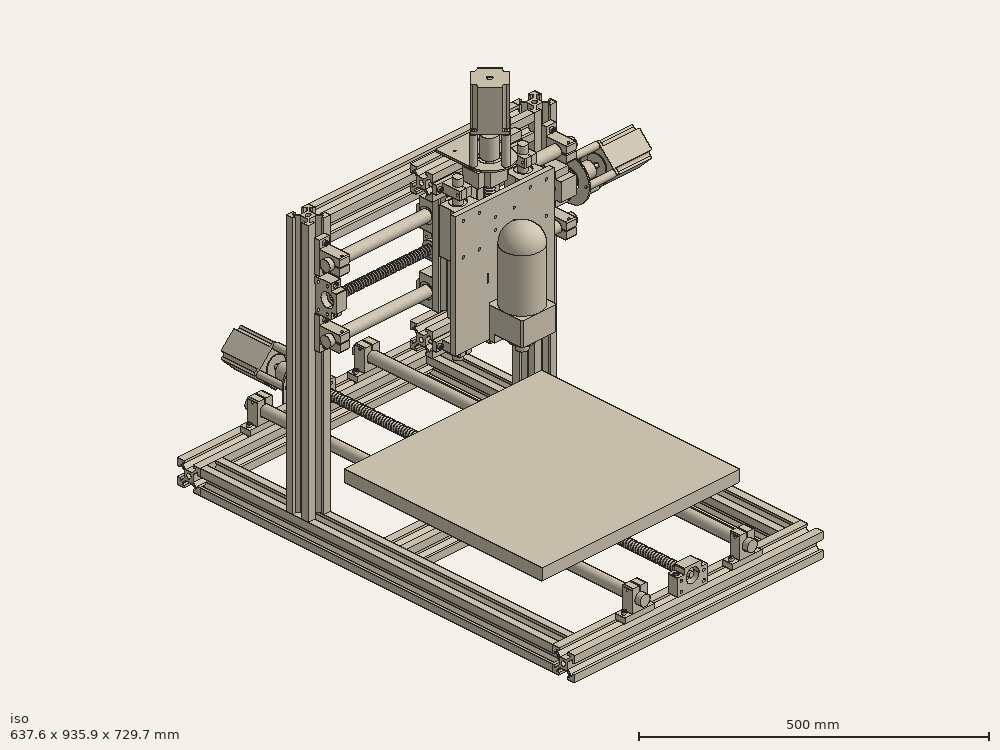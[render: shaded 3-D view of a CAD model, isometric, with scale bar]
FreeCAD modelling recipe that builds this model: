
FCSTD DOCUMENT  (FreeCAD 0.15R4671 (Git))
Label: my_first_cnc
License: CC-BY 3.0
LicenseURL: http://creativecommons.org/licenses/by/3.0/
objects: Part::Feature×111, Part::Cut×42, Part::Cylinder×16, App::DocumentObjectGroup×15, Part::Extrusion×12, PartDesign::Fillet×12, Part::Box×10, Part::Fillet×8, Part::Fuse×1, Part::MultiFuse×1
note: 213 computed .brp shape members not serialized (recipe doc carries the construction recipe); baked Part::Feature solids carry a one-line shape summary decoded from their .brp

FEATURE [Part::Cut] Cut
  Placement = pos=(150,-22,0) rot=(0,0,1;0rad)
FEATURE [Part::Cut] Cut001
  Placement = pos=(40,-22,0) rot=(0,0,1;0rad)
FEATURE [Part::Cut] Cut002
  Placement = pos=(99,-22,0) rot=(0,0,1;0rad)
FEATURE [Part::Cut] Cut003
  Placement = pos=(216,-22,0) rot=(0,0,1;0rad)
FEATURE [Part::Cut] Cut005
  Placement = pos=(332,-22,0) rot=(0,0,1;0rad)
FEATURE [Part::Cut] Cut006
  Placement = pos=(272,-22,0) rot=(0,0,1;0rad)
FEATURE [Part::Extrusion] Extrude002  label="Left"
  Base = -> Cut002
  Dir = (0,0,713)
  Placement = pos=(620.51,-22.0046,-22.0002) rot=(-1,0,0;1.5708rad)
  Solid = false
FEATURE [Part::Cut] Cut004
  Placement = pos=(161,-22,0) rot=(0,0,1;0rad)
FEATURE [Part::Extrusion] Extrude003  label="Right"
  Base = -> Cut004
  Dir = (0,0,713)
  Placement = pos=(1016.51,-22.0045,-22) rot=(-1,0,0;1.5708rad)
  Solid = false
FEATURE [Part::Extrusion] Extrude004  label="Back"
  Base = -> Cut003
  Dir = (0,0,503)
  Placement = pos=(719.51,757.995,260.93) rot=(0,1,0;1.5708rad)
  Solid = false
FEATURE [Part::Extrusion] Extrude005  label="Front"
  Base = -> Cut006
  Dir = (0,0,503)
  Placement = pos=(719.51,-0.00457416,317) rot=(0,1,0;1.5708rad)
  Solid = false
FEATURE [Part::Cut] Cut007
  Placement = pos=(399,-22,0) rot=(0,0,1;0rad)
FEATURE [Part::Cut] Cut008
  Placement = pos=(451,-22,0) rot=(0,0,1;0rad)
FEATURE [Part::Extrusion] Extrude006  label="Inner_base"
  Base = -> Cut005
  Dir = (0,0,413)
  Placement = pos=(764.5,385,377.214) rot=(0,1,0;1.5708rad)
  Solid = false
FEATURE [Part::Extrusion] Extrude009  label="Inner_gantry"
  Dir = (0,0,413)
  Placement = pos=(764.516,538.755,866.83) rot=(0,1,0;1.5708rad)
  Solid = false
FEATURE [Part::Extrusion] Extrude010  label="gantry_left"
  Base = -> Cut007
  Dir = (0,0,490)
  Placement = pos=(320.516,538.755,44.85) rot=(0,0,1;0rad)
  Solid = false
FEATURE [Part::Extrusion] Extrude011  label="gantry_right"
  Base = -> Cut008
  Dir = (0,0,490)
  Placement = pos=(726.5,538.755,44.8) rot=(0,0,1;0rad)
  Solid = false
FEATURE [Part::Cylinder] Cylinder  label="Shaft_Z_Right"
  Angle = 360
  Height = 300
  Placement = pos=(1029.9,347.799,295.468) rot=(0,0,1;0rad)
  Radius = 8
FEATURE [Part::Cylinder] Cylinder001  label="Shaft_Z_Left"
  Angle = 360
  Height = 300
  Placement = pos=(897.986,347.799,294.632) rot=(0,0,1;0rad)
  Radius = 8
FEATURE [Part::Cylinder] Cylinder002  label="Shaft_Y_Top"
  Angle = 360
  Height = 500
  Placement = pos=(722.44,440.799,480.216) rot=(0,1,0;1.5708rad)
  Radius = 10
FEATURE [Part::Cylinder] Cylinder003  label="Shaft_Y_Bottom"
  Angle = 360
  Height = 500
  Placement = pos=(722.44,439.847,355.335) rot=(0,1,0;1.5708rad)
  Radius = 10
FEATURE [Part::Cylinder] Cylinder004  label="Shaft_X_Left"
  Angle = 360
  Height = 800
  Placement = pos=(864.2,-65.0507,76.25) rot=(-1,0,0;1.5708rad)
  Radius = 10
FEATURE [Part::Cylinder] Cylinder005  label="Shaft_X_Right"
  Angle = 360
  Height = 800
  Placement = pos=(1082.5,-64,76.25) rot=(-1,0,0;1.5708rad)
  Radius = 10
FEATURE [Part::Box] Box001
  Height = 10
  Length = 60
  Width = 20
FEATURE [Part::Fuse] Fusion
  Base = -> Box001
FEATURE [Part::Cylinder] Cylinder007
  Angle = 360
  Height = 13
  Placement = pos=(7.5,10,-2) rot=(0,0,1;0rad)
  Radius = 2.3
FEATURE [Part::Cut] Cut010
  Base = -> Fusion
  Tool = -> Cylinder007
FEATURE [Part::Cylinder] Cylinder008
  Angle = 360
  Height = 13
  Placement = pos=(52.5,10,-2) rot=(0,0,1;0rad)
  Radius = 2.3
FEATURE [Part::Cut] Cut011
  Base = -> Cut010
  Tool = -> Cylinder008
FEATURE [Part::Cylinder] Cylinder009
  Angle = 360
  Height = 33
  Placement = pos=(13.1208,9.89392,45.5993) rot=(0,1,0;1.5708rad)
  Radius = 2.3
FEATURE [Part::Cut] Cut012
  Base = -> Cut011
  Tool = -> Cylinder009
FEATURE [Part::Box] Box003
  Height = 15
  Length = 2
  Placement = pos=(29,-2.73,37.37) rot=(0,0,1;0rad)
  Width = 25
FEATURE [Part::Cut] Cut013  label="SK20_X_Front_Left"
  Base = -> Cut012
  Placement = pos=(834.178,-54.56,45.2) rot=(0,0,1;0rad)
  Tool = -> Box003
FEATURE [Part::Cut] Cut014  label="SK020_X_Front_Right"
  Placement = pos=(1051.53,-54.56,45.2) rot=(0,0,1;0rad)
FEATURE [Part::Cut] Cut015  label="SK020_X_Back_Left"
  Placement = pos=(834.409,704.33,45.1) rot=(0,0,1;0rad)
FEATURE [Part::Cut] Cut016  label="SK020_X_Back_Right"
  Placement = pos=(1051.28,704.33,45.1) rot=(0,0,1;0rad)
FEATURE [Part::Cut] Cut017  label="SK020_Y_Bottom_Right"
  Placement = pos=(1190.11,470.93,385) rot=(0.57735,0.57735,-0.57735;2.0944rad)
FEATURE [Part::Cut] Cut018  label="SK020_Y_Top_Right"
  Placement = pos=(1190.95,471.863,510.292) rot=(0.57735,0.57735,-0.57735;2.0944rad)
FEATURE [Part::Cut] Cut019  label="SK020_Y_Bottom_Left"
  Placement = pos=(732.2,471.295,385) rot=(0.57735,0.57735,-0.57735;2.0944rad)
FEATURE [Part::Cut] Cut020  label="SK020_Y_Top_Left"
  Placement = pos=(732.1,471.774,510.292) rot=(0.57735,0.57735,-0.57735;2.0944rad)
FEATURE [Part::Box] Box004  label="Bed"
  Height = 22
  Length = 400
  Placement = pos=(775.334,50.53,98.54) rot=(0,0,1;0rad)
  Width = 400
FEATURE [Part::Feature] M6_Tnut_slot
  Placement = pos=(844.753,-45.1982,38.5832) rot=(0.57735,0.57735,0.57735;2.0944rad)
  shape: bbox 10 x 19.6 x 9.67 mm, 55 faces, 0 solids (baked)
FEATURE [Part::Feature] M6_Tnut_slot001
  Placement = pos=(886.7,-45.8436,38.583) rot=(0.57735,0.57735,0.57735;2.0944rad)
  shape: bbox 10 x 19.6 x 9.67 mm, 55 faces, 0 solids (baked)
FEATURE [Part::Feature] M6_Tnut_slot002
  Placement = pos=(1104.18,-44.84,38.5834) rot=(0.57735,0.57735,0.57735;2.0944rad)
  shape: bbox 10 x 19.6 x 9.67 mm, 55 faces, 0 solids (baked)
FEATURE [Part::Feature] M6_Tnut_slot003
  Placement = pos=(1059,-43.9078,38.5833) rot=(0.57735,0.57735,0.57735;2.0944rad)
  shape: bbox 10 x 19.6 x 9.67 mm, 55 faces, 0 solids (baked)
FEATURE [Part::Feature] M6_Tnut_slot004
  Placement = pos=(841.887,713.889,38.724) rot=(0.57735,0.57735,0.57735;2.0944rad)
  shape: bbox 10 x 19.6 x 9.67 mm, 55 faces, 0 solids (baked)
FEATURE [Part::Feature] M6_Tnut_slot005
  Placement = pos=(1200.15,477.74,332.424) rot=(0,0,1;3.14159rad)
  shape: bbox 19.6 x 9.67 x 10 mm, 55 faces, 0 solids (baked)
FEATURE [Part::Feature] M6_Tnut_slot006
  Placement = pos=(887.231,713.888,38.7233) rot=(0.57735,0.57735,0.57735;2.0944rad)
  shape: bbox 10 x 19.6 x 9.67 mm, 55 faces, 0 solids (baked)
FEATURE [Part::Feature] M6_Tnut_slot007
  Placement = pos=(1058.64,714.392,38.7233) rot=(0.57735,0.57735,0.57735;2.0944rad)
  shape: bbox 10 x 19.6 x 9.67 mm, 55 faces, 0 solids (baked)
FEATURE [Part::Feature] M6_Tnut_slot008
  Placement = pos=(1103.91,714.392,38.7233) rot=(0.57735,0.57735,0.57735;2.0944rad)
  shape: bbox 10 x 19.6 x 9.67 mm, 55 faces, 0 solids (baked)
FEATURE [Part::Feature] M6_Tnut_slot009
  Placement = pos=(1200.11,477.74,377.562) rot=(0,0,1;3.14159rad)
  shape: bbox 19.6 x 9.67 x 10 mm, 55 faces, 0 solids (baked)
FEATURE [Part::Feature] M6_Tnut_slot010
  Placement = pos=(1200.95,476.213,457.743) rot=(0,0,1;3.14159rad)
  shape: bbox 19.6 x 9.67 x 10 mm, 55 faces, 0 solids (baked)
FEATURE [Part::Feature] M6_Tnut_slot011
  Placement = pos=(1200.95,476.213,502.749) rot=(0,0,1;3.14159rad)
  shape: bbox 19.6 x 9.67 x 10 mm, 55 faces, 0 solids (baked)
FEATURE [Part::Feature] M6_Tnut_slot012
  Placement = pos=(742.302,476.923,502.73) rot=(0,0,1;3.14159rad)
  shape: bbox 19.6 x 9.67 x 10 mm, 55 faces, 0 solids (baked)
FEATURE [Part::Feature] M6_Tnut_slot013
  Placement = pos=(742.504,477.741,457.628) rot=(0,0,1;3.14159rad)
  shape: bbox 19.6 x 9.67 x 10 mm, 55 faces, 0 solids (baked)
FEATURE [Part::Feature] M6_Tnut_slot014
  Placement = pos=(742.302,477.742,376.507) rot=(0,0,1;3.14159rad)
  shape: bbox 19.6 x 9.67 x 10 mm, 55 faces, 0 solids (baked)
FEATURE [Part::Feature] M6_Tnut_slot015
  Placement = pos=(742.328,477.738,332.439) rot=(0,0,1;3.14159rad)
  shape: bbox 19.6 x 9.67 x 10 mm, 55 faces, 0 solids (baked)
FEATURE [Part::Cut] Cut021  label="Cut013"
  Placement = pos=(220,-22,0) rot=(0,0,1;0rad)
FEATURE [Part::Cut] Cut022  label="Cut014"
  Placement = pos=(-22,-22,0) rot=(0,0,1;0rad)
FEATURE [Part::Extrusion] Extrude013  label="Right_Z"
  Base = -> Cut001
  Dir = (0,0,213)
  Placement = pos=(924.038,442,336.783) rot=(0,0,1;0rad)
  Solid = false
FEATURE [Part::Extrusion] Extrude014  label="Left_Z"
  Base = -> Cut022
  Dir = (0,0,213)
  Placement = pos=(940.038,442,336.783) rot=(0,0,1;0rad)
  Solid = false
FEATURE [Part::Cut] Cut036  label="SC20VUU004"
  Placement = pos=(955,420,507.314) rot=(0.57735,-0.57735,-0.57735;4.18879rad)
FEATURE [Part::Cut] Cut037  label="SC20VUU005"
  Placement = pos=(1000.5,420,507.275) rot=(0.57735,-0.57735,-0.57735;4.18879rad)
FEATURE [Part::Cut] Cut038  label="SC20VUU006"
  Placement = pos=(955,420,382.628) rot=(0.57735,-0.57735,-0.57735;4.18879rad)
FEATURE [Part::Cut] Cut039  label="SC20VUU007"
  Placement = pos=(1000.5,420,382.412) rot=(0.57735,-0.57735,-0.57735;4.18879rad)
FEATURE [Part::Cut] Cut040  label="Cut032"
  Placement = pos=(54.0681,-22,14.7162) rot=(0,0,1;0rad)
FEATURE [Part::Cut] Cut041  label="Cut033"
  Placement = pos=(-24.4873,-22.0001,-16.5816) rot=(0,0,1;0rad)
FEATURE [Part::Extrusion] Extrude016  label="Top_Z"
  Base = -> Cut040
  Dir = (0,0,180)
  Placement = pos=(859.038,442,649.933) rot=(0,1,0;1.5708rad)
  Solid = false
FEATURE [Part::Extrusion] Extrude017  label="Bottom_Z"
  Base = -> Cut041
  Dir = (0,0,180)
  Placement = pos=(890.317,442,312.344) rot=(0,1,0;1.5708rad)
  Solid = false
FEATURE [PartDesign::Fillet] Fillet
  Base = -> Cut020 [Edge39]
  Radius = 2
FEATURE [PartDesign::Fillet] Fillet001
  Base = -> Fillet [Edge35]
  Radius = 2
FEATURE [PartDesign::Fillet] Fillet004
  Base = -> Cut018 [Edge39]
  Radius = 2
FEATURE [PartDesign::Fillet] Fillet005
  Base = -> Fillet004 [Edge35]
  Radius = 2
FEATURE [PartDesign::Fillet] Fillet008
  Base = -> Cut015 [Edge52]
  Placement = pos=(834.409,704.33,45.1) rot=(0,0,1;0rad)
  Radius = 2
FEATURE [PartDesign::Fillet] Fillet009
  Base = -> Fillet008 [Edge28]
  Placement = pos=(834.409,704.33,45.1) rot=(0,0,1;0rad)
  Radius = 2
FEATURE [PartDesign::Fillet] Fillet010
  Base = -> Cut016 [Edge39]
  Placement = pos=(1051.28,704.33,45.1) rot=(0,0,1;0rad)
  Radius = 2
FEATURE [PartDesign::Fillet] Fillet011
  Base = -> Fillet010 [Edge35]
  Placement = pos=(1051.28,704.33,45.1) rot=(0,0,1;0rad)
  Radius = 2
FEATURE [PartDesign::Fillet] Fillet012
  Base = -> Cut014 [Edge52]
  Placement = pos=(1051.53,-54.56,45.2) rot=(0,0,1;0rad)
  Radius = 2
FEATURE [PartDesign::Fillet] Fillet013
  Base = -> Fillet012 [Edge28]
  Placement = pos=(1051.53,-54.56,45.2) rot=(0,0,1;0rad)
  Radius = 2
FEATURE [PartDesign::Fillet] Fillet014
  Base = -> Cut013 [Edge52]
  Placement = pos=(834.178,-54.56,45.2) rot=(0,0,1;0rad)
  Radius = 2
FEATURE [PartDesign::Fillet] Fillet015
  Base = -> Fillet014 [Edge28]
  Placement = pos=(834.178,-54.56,45.2) rot=(0,0,1;0rad)
  Radius = 2
FEATURE [Part::Fillet] Fillet001002
  Edges = 1 edges r=2: [Edge27]
  Placement = pos=(1053.67,374.8,581.619) rot=(0,0.707107,-0.707107;3.14159rad)
FEATURE [Part::Fillet] Fillet001003
  Edges = 1 edges r=2: [Edge27]
  Placement = pos=(921.74,374.8,322.412) rot=(0,0.707107,-0.707107;3.14159rad)
FEATURE [Part::Fillet] Fillet001004
  Edges = 1 edges r=2: [Edge27]
  Placement = pos=(1053.77,374.8,322.519) rot=(0,0.707107,-0.707107;3.14159rad)
FEATURE [Part::Fillet] Fillet001005
  Edges = 1 edges r=2: [Edge27]
  Placement = pos=(921.98,374.8,581.619) rot=(0,0.707107,-0.707107;3.14159rad)
FEATURE [Part::Box] Box012
  Height = 32.5
  Length = 50
  Width = 85
FEATURE [Part::Cylinder] Cylinder015
  Angle = 360
  Height = 100
  Placement = pos=(25,-4.78696,19) rot=(-1,0,0;1.5708rad)
  Radius = 8.1
FEATURE [Part::Cut] Cut042
  Base = -> Box012
  Tool = -> Cylinder015
FEATURE [Part::Box] Box001001
  Height = 6
  Length = 25
  Placement = pos=(-43.8255,-3.33042e-05,2.24746) rot=(0,0,1;0rad)
  Width = 85
FEATURE [Part::Box] Box002001
  Height = 10
  Length = 10
  Placement = pos=(-50.8986,-3,9.31859) rot=(0,1,0;0.785397rad)
  Width = 90
FEATURE [Part::Cut] Cut001001
  Base = -> Box001001
  Tool = -> Box002001
FEATURE [Part::Box] Box003001
  Height = 10
  Length = 10
  Placement = pos=(-18.82,-2,2.25) rot=(0,-1,0;0.785397rad)
  Width = 90
FEATURE [Part::Cut] Cut002001
  Base = -> Cut001001
  Placement = pos=(56.6969,-0.000184233,30.2) rot=(0,0,1;0rad)
  Tool = -> Box003001
FEATURE [Part::MultiFuse] Fusion002
  Shapes = -> [Cut042,Cut002001]
FEATURE [Part::Box] Box004001
  Height = 23.5
  Length = 1
  Placement = pos=(0,0,9) rot=(0,0,1;0rad)
  Width = 85
FEATURE [Part::Cut] Cut003001
  Base = -> Fusion002
  Tool = -> Box004001
FEATURE [Part::Box] Box005001
  Height = 23.5
  Length = 1
  Placement = pos=(49,0,9) rot=(0,0,1;0rad)
  Width = 85
FEATURE [Part::Cut] Cut004001
  Base = -> Cut003001
  Tool = -> Box005001
FEATURE [Part::Cylinder] Cylinder001001
  Angle = 360
  Height = 40
  Placement = pos=(7,12.5,-2) rot=(0,0,1;0rad)
  Radius = 2.3
FEATURE [Part::Cut] Cut005001
  Base = -> Cut004001
  Tool = -> Cylinder001001
FEATURE [Part::Cylinder] Cylinder002001
  Angle = 360
  Height = 40
  Placement = pos=(7,72.5,-3) rot=(0,0,1;0rad)
  Radius = 2.3
FEATURE [Part::Cut] Cut006001
  Base = -> Cut005001
  Tool = -> Cylinder002001
FEATURE [Part::Cylinder] Cylinder003001
  Angle = 360
  Height = 40
  Placement = pos=(43,12.5,-4) rot=(0,0,1;0rad)
  Radius = 2
FEATURE [Part::Cut] Cut007001
  Base = -> Cut006001
  Tool = -> Cylinder003001
FEATURE [Part::Cylinder] Cylinder004001
  Angle = 360
  Height = 40
  Placement = pos=(43,72.5,-4) rot=(0,0,1;0rad)
  Radius = 2.3
FEATURE [Part::Cut] Cut008001
  Base = -> Cut007001
  Tool = -> Cylinder004001
FEATURE [Part::Cylinder] Cylinder005001
  Angle = 360
  Height = 3
  Placement = pos=(25.5737,-1,19.0038) rot=(-1,0,0;1.5708rad)
  Radius = 14
FEATURE [Part::Cut] Cut009001
  Base = -> Cut008001
  Tool = -> Cylinder005001
FEATURE [Part::Cut] Cut010001
  Base = -> Cut009001
  Tool = -> Cylinder005001
FEATURE [Part::Cylinder] Cylinder006001
  Angle = 360
  Height = 3
  Placement = pos=(25.6346,83,19.0294) rot=(-1,0,0;1.5708rad)
  Radius = 14
FEATURE [Part::Cut] Cut011001
  Base = -> Cut010001
  Placement = pos=(872.932,328.758,552.688) rot=(-1,0,0;1.5708rad)
  Tool = -> Cylinder006001
FEATURE [Part::Cut] Cut011002
  Placement = pos=(1004.97,328.822,552.619) rot=(-1,0,0;1.5708rad)
FEATURE [Part::Feature] M6_Tnut_slot10
  Placement = pos=(879.631,381.008,573.739) rot=(0.707107,0,0.707107;3.14159rad)
  shape: bbox 10 x 9.67 x 19.6 mm, 55 faces, 0 solids (baked)
FEATURE [Part::Feature] M6_Tnut_slot016
  Placement = pos=(916.2,381.031,573.724) rot=(0.707107,0,0.707107;3.14159rad)
  shape: bbox 10 x 9.67 x 19.6 mm, 55 faces, 0 solids (baked)
FEATURE [Part::Feature] M6_Tnut_slot017
  Placement = pos=(1011.45,381.019,573.726) rot=(0.707107,0,0.707107;3.14159rad)
  shape: bbox 10 x 9.67 x 19.6 mm, 55 faces, 0 solids (baked)
FEATURE [Part::Feature] M6_Tnut_slot018
  Placement = pos=(1047.94,381.016,573.724) rot=(0.707107,0,0.707107;3.14159rad)
  shape: bbox 10 x 9.67 x 19.6 mm, 55 faces, 0 solids (baked)
FEATURE [Part::Feature] M6_Tnut_slot020
  Placement = pos=(879.473,380.903,314.506) rot=(0.707107,0,0.707107;3.14159rad)
  shape: bbox 10 x 9.67 x 19.6 mm, 55 faces, 0 solids (baked)
FEATURE [Part::Feature] M6_Tnut_slot021
  Placement = pos=(916.005,380.953,314.519) rot=(0.707107,0,0.707107;3.14159rad)
  shape: bbox 10 x 9.67 x 19.6 mm, 55 faces, 0 solids (baked)
FEATURE [Part::Feature] M6_Tnut_slot022
  Placement = pos=(1011.52,380.955,314.598) rot=(0.707107,0,0.707107;3.14159rad)
  shape: bbox 10 x 9.67 x 19.6 mm, 55 faces, 0 solids (baked)
FEATURE [Part::Feature] M6_Tnut_slot023
  Placement = pos=(1048.04,380.934,314.688) rot=(0.707107,0,0.707107;3.14159rad)
  shape: bbox 10 x 9.67 x 19.6 mm, 55 faces, 0 solids (baked)
FEATURE [Part::Feature] M6_Tnut_slot024
  Placement = pos=(986.716,413.96,459.779) rot=(0,0,1;0rad)
  shape: bbox 19.6 x 9.67 x 10 mm, 55 faces, 0 solids (baked)
FEATURE [Part::Feature] M6_Tnut_slot025
  Placement = pos=(986.711,413.96,500.798) rot=(0,0,1;0rad)
  shape: bbox 19.6 x 9.67 x 10 mm, 55 faces, 0 solids (baked)
FEATURE [Part::Feature] M6_Tnut_slot026
  Placement = pos=(941.238,413.955,500.893) rot=(0,0,1;0rad)
  shape: bbox 19.6 x 9.67 x 10 mm, 55 faces, 0 solids (baked)
FEATURE [Part::Feature] M6_Tnut_slot027
  Placement = pos=(941.292,413.965,459.839) rot=(0,0,1;0rad)
  shape: bbox 19.6 x 9.67 x 10 mm, 55 faces, 0 solids (baked)
FEATURE [Part::Feature] M6_Tnut_slot028
  Placement = pos=(986.758,413.959,375.695) rot=(0,0,1;0rad)
  shape: bbox 19.6 x 9.67 x 10 mm, 55 faces, 0 solids (baked)
FEATURE [Part::Feature] M6_Tnut_slot029
  Placement = pos=(986.679,413.961,335.402) rot=(0,0,1;0rad)
  shape: bbox 19.6 x 9.67 x 10 mm, 55 faces, 0 solids (baked)
FEATURE [Part::Feature] M6_Tnut_slot030
  Placement = pos=(941.357,413.961,376.087) rot=(0,0,1;0rad)
  shape: bbox 19.6 x 9.67 x 10 mm, 55 faces, 0 solids (baked)
FEATURE [Part::Feature] M6_Tnut_slot031
  Placement = pos=(941.312,413.956,335.16) rot=(0,0,1;0rad)
  shape: bbox 19.6 x 9.67 x 10 mm, 55 faces, 0 solids (baked)
FEATURE [Part::Feature] ISO4762_M5x20_
  Placement = pos=(1104.13,-44.63,55.35) rot=(0,0,1;0rad)
  shape: bbox 9.2 x 9.2 x 25 mm, 23 faces (baked)
FEATURE [Part::Feature] ISO4762_M5x20_001
  Placement = pos=(1058.54,-44.63,55.35) rot=(0,0,1;0rad)
  shape: bbox 9.2 x 9.2 x 25 mm, 23 faces (baked)
FEATURE [Part::Feature] ISO4762_M5x20_002
  Placement = pos=(887.559,-44.6308,55.35) rot=(0,0,1;0rad)
  shape: bbox 9.2 x 9.2 x 25 mm, 23 faces (baked)
FEATURE [Part::Feature] ISO4762_M5x20_003
  Placement = pos=(841.861,-44.6304,55.35) rot=(0,0,1;0rad)
  shape: bbox 9.2 x 9.2 x 25 mm, 23 faces (baked)
FEATURE [Part::Feature] ISO4762_M5x20_004
  Placement = pos=(1103.9,714.044,55.2898) rot=(0,0,1;0rad)
  shape: bbox 9.2 x 9.2 x 25 mm, 23 faces (baked)
FEATURE [Part::Feature] ISO4762_M5x20_005
  Placement = pos=(1057.98,714.049,55.4021) rot=(0,0,1;0rad)
  shape: bbox 9.2 x 9.2 x 25 mm, 23 faces (baked)
FEATURE [Part::Feature] ISO4762_M5x20_006
  Placement = pos=(886.949,714.123,55.3565) rot=(0,0,1;0rad)
  shape: bbox 9.2 x 9.2 x 25 mm, 23 faces (baked)
FEATURE [Part::Feature] ISO4762_M5x20_007
  Placement = pos=(841.94,714.052,55.283) rot=(0,0,1;0rad)
  shape: bbox 9.2 x 9.2 x 25 mm, 23 faces (baked)
FEATURE [Part::Feature] ISO4762_M5x20_008
  Placement = pos=(1200.95,461.863,502.419) rot=(1,0,0;1.5708rad)
  shape: bbox 9.2 x 25 x 9.2 mm, 23 faces (baked)
FEATURE [Part::Feature] ISO4762_M5x20_009
  Placement = pos=(1200.95,461.663,457.226) rot=(1,0,0;1.5708rad)
  shape: bbox 9.2 x 25 x 9.2 mm, 23 faces (baked)
FEATURE [Part::Feature] ISO4762_M5x20_010
  Placement = pos=(742.076,462.099,502.511) rot=(1,0,0;1.5708rad)
  shape: bbox 9.2 x 25 x 9.2 mm, 23 faces (baked)
FEATURE [Part::Feature] ISO4762_M5x20_011
  Placement = pos=(742.071,462.002,457.208) rot=(1,0,0;1.5708rad)
  shape: bbox 9.2 x 25 x 9.2 mm, 23 faces (baked)
FEATURE [Part::Feature] ISO4762_M5x20_012
  Placement = pos=(742.121,461.12,376.304) rot=(1,0,0;1.5708rad)
  shape: bbox 9.2 x 25 x 9.2 mm, 23 faces (baked)
FEATURE [Part::Feature] ISO4762_M5x20_013
  Placement = pos=(742.163,461.12,332.014) rot=(1,0,0;1.5708rad)
  shape: bbox 9.2 x 25 x 9.2 mm, 23 faces (baked)
FEATURE [Part::Feature] ISO4762_M5x20_014
  Placement = pos=(1200,461.12,377.476) rot=(1,0,0;1.5708rad)
  shape: bbox 9.2 x 25 x 9.2 mm, 23 faces (baked)
FEATURE [Part::Feature] ISO4762_M5x20_015
  Placement = pos=(1200.11,461.099,332.483) rot=(1,0,0;1.5708rad)
  shape: bbox 9.2 x 25 x 9.2 mm, 23 faces (baked)
FEATURE [Part::Feature] ISO4762_M5x20_016
  Placement = pos=(879.79,366.7,573.653) rot=(1,0,0;1.5708rad)
  shape: bbox 9.2 x 25 x 9.2 mm, 23 faces (baked)
FEATURE [Part::Feature] ISO4762_M5x20_017
  Placement = pos=(916.367,366.7,573.47) rot=(1,0,0;1.5708rad)
  shape: bbox 9.2 x 25 x 9.2 mm, 23 faces (baked)
FEATURE [Part::Feature] ISO4762_M5x20_018
  Placement = pos=(1011.46,366.7,573.505) rot=(1,0,0;1.5708rad)
  shape: bbox 9.2 x 25 x 9.2 mm, 23 faces (baked)
FEATURE [Part::Feature] ISO4762_M5x20_019
  Placement = pos=(1047.88,366.7,573.7) rot=(1,0,0;1.5708rad)
  shape: bbox 9.2 x 25 x 9.2 mm, 23 faces (baked)
FEATURE [Part::Feature] ISO4762_M5x20_020
  Placement = pos=(879.525,366.7,314.408) rot=(1,0,0;1.5708rad)
  shape: bbox 9.2 x 25 x 9.2 mm, 23 faces (baked)
FEATURE [Part::Feature] ISO4762_M5x20_021
  Placement = pos=(915.996,366.7,314.466) rot=(1,0,0;1.5708rad)
  shape: bbox 9.2 x 25 x 9.2 mm, 23 faces (baked)
FEATURE [Part::Feature] ISO4762_M5x20_022
  Placement = pos=(1011.46,366.7,314.503) rot=(1,0,0;1.5708rad)
  shape: bbox 9.2 x 25 x 9.2 mm, 23 faces (baked)
FEATURE [Part::Feature] ISO4762_M5x20_023
  Placement = pos=(1048.08,366.7,314.536) rot=(1,0,0;1.5708rad)
  shape: bbox 9.2 x 25 x 9.2 mm, 23 faces (baked)
FEATURE [Part::Box] Box005002  label="Cube"
  Height = 10
  Length = 361
  Placement = pos=(795.534,71.3936,98.4922) rot=(0,0,1;0rad)
  Width = 361
FEATURE [Part::Cut] Cut011005  label="Spoilboard_Bed"
  Base = -> Box004
  Placement = pos=(-4.73697,-1.00343,1.16107) rot=(0,0,1;0rad)
  Tool = -> Box005002
FEATURE [Part::Feature] Pad001  label="Motor_X"
  Placement = pos=(972.86,868.93,69.8262) rot=(0.382683,0,0.92388;3.14159rad)
  shape: bbox 79.62 x 102 x 79.62 mm, 34 faces (baked)
FEATURE [Part::Feature] Pad002  label="Motor_Y"
  Placement = pos=(1357.09,446.522,417.405) rot=(0.357407,-0.357407,0.862856;1.71777rad)
  shape: bbox 102 x 79.62 x 79.62 mm, 34 faces (baked)
FEATURE [Part::Feature] Pad  label="Motor_Z"
  Placement = pos=(964.751,349.979,729.656) rot=(-0.862856,-0.357407,0.357407;1.71777rad)
  shape: bbox 79.62 x 79.62 x 102 mm, 34 faces (baked)
FEATURE [Part::Feature] Part__Feature  label="BF12_Z"
  Placement = pos=(964.673,349.918,314.167) rot=(0,0,1;3.14159rad)
  shape: bbox 60 x 43 x 20 mm, 48 faces (baked)
FEATURE [Part::Feature] Part__Feature001  label="BF12_X"
  Placement = pos=(971.01,-44.5,70.0662) rot=(0,0.707107,0.707107;3.14159rad)
  shape: bbox 60 x 20 x 43 mm, 48 faces (baked)
FEATURE [Part::Feature] Part__Feature002  label="BF12_Y"
  Placement = pos=(742.761,446.587,417.281) rot=(0.707107,0.001737,0.707104;3.14159rad)
  shape: bbox 20.11 x 43.16 x 60.08 mm, 48 faces (baked)
FEATURE [Part::Feature] Pocket  label="Motor_Holder_X"
  Placement = pos=(973.206,738.696,-0.0697632) rot=(1,0,0;1.5708rad)
  shape: bbox 80 x 2.7 x 110.1 mm, 12 faces (baked)
FEATURE [Part::Feature] Pocket001  label="Motor_Holder_Z"
  Placement = pos=(964.724,420.024,598.846) rot=(1,0,0;3.14159rad)
  shape: bbox 80 x 110.1 x 2.7 mm, 12 faces (baked)
FEATURE [Part::Feature] Pocket002  label="Motor_Holder_Y"
  Placement = pos=(1222.9,516.706,417.427) rot=(0.707107,0,0.707107;3.14159rad)
  shape: bbox 2.7 x 110.1 x 80 mm, 12 faces (baked)
FEATURE [Part::Fillet] Fillet001006
  Base = -> Cut017
  Edges = 1 edges r=2: [Edge39]
FEATURE [Part::Fillet] Fillet001007
  Base = -> Fillet001006
  Edges = 1 edges r=2: [Edge35]
FEATURE [Part::Fillet] Fillet001008
  Base = -> Cut019
  Edges = 1 edges r=2: [Edge52]
FEATURE [Part::Fillet] Fillet001009
  Base = -> Fillet001008
  Edges = 1 edges r=2: [Edge28]
FEATURE [Part::Feature] Pocket003  label="Router"
  Placement = pos=(964.205,318.53,338.088) rot=(0,0,1;3.14159rad)
  shape: bbox 70 x 70 x 208.5 mm, 23 faces (baked)
FEATURE [App::DocumentObjectGroup] Group  label="Base"
  Group = -> [Extrude002,Extrude003,Extrude004,Extrude005,Extrude006,Fillet015,Fillet013,Fillet009,Fillet011,ISO4762_M5x20_007,M6_Tnut_slot004,ISO4762_M5x20_006,M6_Tnut_slot006,M6_Tnut_slot007,ISO4762_M5x20_005,M6_Tnut_slot008,ISO4762_M5x20_004,ISO4762_M5x20_003,M6_Tnut_slot,ISO4762_M5x20_002,M6_Tnut_slot001,ISO4762_M5x20_001,M6_Tnut_slot003,ISO4762_M5x20_,M6_Tnut_slot002]
FEATURE [App::DocumentObjectGroup] Group001  label="Gantry"
  Group = -> [Extrude009,Extrude010,Extrude011,Fillet001,Fillet005,Fillet001007,Fillet001009,ISO4762_M5x20_010,M6_Tnut_slot012,ISO4762_M5x20_011,M6_Tnut_slot013,ISO4762_M5x20_008,M6_Tnut_slot011,ISO4762_M5x20_009,M6_Tnut_slot010,ISO4762_M5x20_012,M6_Tnut_slot014,ISO4762_M5x20_013,M6_Tnut_slot015,ISO4762_M5x20_014,M6_Tnut_slot009,ISO4762_M5x20_015,M6_Tnut_slot005]
FEATURE [App::DocumentObjectGroup] Group003  label="Head"
  Group = -> [Extrude016,Extrude017,Extrude013,Extrude014,Fillet001005,Fillet001002,Fillet001003,Fillet001004,ISO4762_M5x20_016,M6_Tnut_slot10,M6_Tnut_slot016,ISO4762_M5x20_018,M6_Tnut_slot017,ISO4762_M5x20_019,M6_Tnut_slot018,ISO4762_M5x20_020,M6_Tnut_slot020,ISO4762_M5x20_021,M6_Tnut_slot021,ISO4762_M5x20_022,M6_Tnut_slot022,ISO4762_M5x20_023,M6_Tnut_slot023,ISO4762_M5x20_017]
FEATURE [Part::Feature] Clone001  label="BK12_X"
  Placement = pos=(17755.1,993.452,-176.664) rot=(0,0.707107,0.707107;3.14159rad)
  shape: bbox 60 x 30.48 x 42.95 mm, 19 faces (baked)
FEATURE [App::DocumentObjectGroup] Group009  label="GuideY"
  Group = -> [Cylinder002,Cylinder003,Cut037,Cut039,Cut036,Cut038,M6_Tnut_slot026,M6_Tnut_slot025,M6_Tnut_slot027,M6_Tnut_slot024,M6_Tnut_slot030,M6_Tnut_slot028,M6_Tnut_slot031,M6_Tnut_slot029]
FEATURE [App::DocumentObjectGroup] Group010  label="GuideZ"
  Group = -> [Cylinder001,Cylinder,Cut011001,Cut011002]
FEATURE [App::DocumentObjectGroup] Group014  label="Hidden_Primitives"
  Group = -> [Cut013,Cut014,Cut015,Cut016,Fillet,Fillet004,Fillet014,Fillet008,Fillet010,Fillet012,Cut018,Cut020,Cut,Cut021]
FEATURE [Part::Feature] Pocket004  label="Ballnut_House"
  Placement = pos=(970.787,265.863,89.6918) rot=(0,-0.707106,0.707107;3.14159rad)
  shape: bbox 47.5 x 34 x 39 mm, 21 faces (baked)
FEATURE [Part::Feature] Pocket008  label="Ballnut_House_Y"
  Placement = pos=(980.343,427.18,417.308) rot=(0,-1,0;1.5708rad)
  shape: bbox 34 x 39 x 47.5 mm, 21 faces (baked)
FEATURE [Part::Feature] Fusion007  label="RM1605_800mm"
  Placement = pos=(971.089,-40.9765,69.9617) rot=(0.57735,-0.57735,-0.57735;4.18879rad)
  shape: bbox 48 x 803 x 40 mm, 319 faces (baked)
FEATURE [Part::Feature] Fusion009  label="RM1605_500mm"
  Placement = pos=(753.889,446.569,417.279) rot=(0.57735,0.57735,0.57735;2.0944rad)
  shape: bbox 503 x 40 x 48 mm, 220 faces, 2 solids (baked)
FEATURE [Part::Feature] Pocket011  label="Ballnut_house_supportY"
  Placement = pos=(946.399,431.842,417.123) rot=(0.57735,0.57735,-0.57735;2.0944rad)
  shape: bbox 44.1 x 12.15 x 57.6 mm, 18 faces (baked)
FEATURE [Part::Feature] Clone002  label="BK12_Y"
  Placement = pos=(1481.85,693.131,-16367.1) rot=(0.707107,0,0.707107;3.14159rad)
  shape: bbox 30.48 x 42.95 x 60 mm, 19 faces (baked)
FEATURE [App::DocumentObjectGroup] Group006  label="BallScrewY"
  Group = -> [Part__Feature002,Pocket008,Fusion009,Pocket011,Clone002]
FEATURE [Part::Feature] Clone  label="BK12_Z"
  Placement = pos=(17749.1,596.677,854.729) rot=(0,0,1;3.14159rad)
  shape: bbox 60 x 42.95 x 30.48 mm, 19 faces (baked)
FEATURE [Part::Feature] Fusion010  label="RM1605_300mm"
  Placement = pos=(964.868,349.99,322.226) rot=(0,0,1;1.5708rad)
  shape: bbox 48 x 40 x 303 mm, 135 faces, 2 solids (baked)
FEATURE [Part::Feature] Pocket013  label="Ballnut_House_Z"
  Placement = pos=(964.876,330.002,467.838) rot=(0,1,0;3.14159rad)
  shape: bbox 47.5 x 39 x 34 mm, 21 faces (baked)
FEATURE [App::DocumentObjectGroup] Group007  label="BallScrewZ"
  Group = -> [Part__Feature,Clone,Pocket013,Fusion010]
FEATURE [Part::Feature] Pocket015  label="Bed_Metal"
  Placement = pos=(971.325,250.659,99.3871) rot=(0,0,1;0rad)
  shape: bbox 360 x 360 x 10 mm, 30 faces (baked)
FEATURE [Part::Feature] Pad009  label="Plate_Z"
  Placement = pos=(964.269,328.708,323.161) rot=(1,0,0;1.5708rad)
  shape: bbox 200 x 10 x 230 mm, 27 faces (baked)
FEATURE [App::DocumentObjectGroup] Group004  label="Spinder"
  Group = -> [Pocket003,Pad009]
FEATURE [Part::Feature] Pocket018  label="Ballnut_House_Support"
  Placement = pos=(970.767,231.873,85.0723) rot=(0,0,1;0rad)
  shape: bbox 58 x 45 x 14.15 mm, 33 faces (baked)
FEATURE [App::DocumentObjectGroup] Group005  label="BallScrewX"
  Group = -> [Part__Feature001,Clone001,Pocket004,Fusion007,Pocket018]
FEATURE [Part::Feature] Pocket019  label="Coupler_Z"
  Placement = pos=(964.75,350.03,637.522) rot=(1,0,0;3.14159rad)
  shape: bbox 28 x 28 x 38 mm, 6 faces (baked)
FEATURE [Part::Feature] Pocket020  label="Coupler_Y"
  Placement = pos=(1263.93,446.656,417.213) rot=(0,-1,0;1.5708rad)
  shape: bbox 38 x 28 x 28 mm, 6 faces (baked)
FEATURE [Part::Feature] Pocket021  label="Coupler_X"
  Placement = pos=(970.874,776.108,69.9546) rot=(1,0,0;1.5708rad)
  shape: bbox 28 x 38 x 28 mm, 6 faces (baked)
FEATURE [Part::Feature] Pocket022  label="SpacerZ1"
  Placement = pos=(998.1,350.071,598.847) rot=(0,0,-1;0.769218rad)
  shape: bbox 12 x 12 x 52.5 mm, 4 faces (baked)
FEATURE [Part::Feature] Pocket023  label="SpacerZ2"
  Placement = pos=(931.435,350.049,598.848) rot=(0,0,-1;0.769218rad)
  shape: bbox 12 x 12 x 52.5 mm, 4 faces (baked)
FEATURE [Part::Feature] Pocket024  label="SpacerZ3"
  Placement = pos=(964.583,316.598,598.848) rot=(0,0,-1;0.769218rad)
  shape: bbox 12 x 12 x 52.5 mm, 4 faces (baked)
FEATURE [App::DocumentObjectGroup] Group013  label="MotorZ"
  Group = -> [Pad,Pocket001,Pocket019,Pocket022,Pocket023,Pocket024]
FEATURE [Part::Feature] Pocket025  label="SpacerY1"
  Placement = pos=(1225.6,446.298,383.873) rot=(0.294306,0.909268,0.294306;1.66577rad)
  shape: bbox 52.5 x 12 x 12 mm, 4 faces (baked)
FEATURE [Part::Feature] Pocket026  label="SpacerY2"
  Placement = pos=(1225.6,446.376,450.752) rot=(0.705682,0.063442,0.705682;3.01488rad)
  shape: bbox 52.5 x 12 x 12 mm, 4 faces (baked)
FEATURE [Part::Feature] Pocket027  label="SpacerY3"
  Placement = pos=(1278.1,413.149,417.459) rot=(-0.436659,-0.786548,0.436659;1.80862rad)
  shape: bbox 52.5 x 12 x 12 mm, 4 faces (baked)
FEATURE [App::DocumentObjectGroup] Group012  label="MotorY"
  Group = -> [Pad002,Pocket002,Pocket020,Pocket025,Pocket026,Pocket027]
FEATURE [Part::Feature] Pocket028  label="SpacerX1"
  Placement = pos=(1006.2,738.695,69.7669) rot=(-0.122842,0.701751,0.701751;2.89713rad)
  shape: bbox 12 x 52.5 x 12 mm, 4 faces (baked)
FEATURE [Part::Feature] Pocket029  label="SpacerX2"
  Placement = pos=(939.69,738.703,69.7679) rot=(-0.908498,-0.29569,-0.295294;1.668rad)
  shape: bbox 12 x 52.52 x 12.07 mm, 4 faces (baked)
FEATURE [Part::Feature] Pocket030  label="SpacerX3"
  Placement = pos=(972.889,791.196,103.137) rot=(-0.57368,0.579177,-0.579177;4.18328rad)
  shape: bbox 12 x 52.5 x 12 mm, 4 faces (baked)
FEATURE [App::DocumentObjectGroup] Group011  label="MotorX"
  Group = -> [Pad001,Pocket,Pocket021,Pocket028,Pocket029,Pocket030]
FEATURE [Part::Feature] ISO4762_M5x16_  label="ISO4762_M5x16_016"
  Placement = pos=(842.249,110.269,105.239) rot=(0,0,1;0rad)
  shape: bbox 8.5 x 8.5 x 21 mm, 23 faces (baked)
FEATURE [Part::Feature] ISO4762_M5x16_001  label="ISO4762_M5x16_017"
  Placement = pos=(877.227,110.528,105.186) rot=(0,0,1;0rad)
  shape: bbox 8.5 x 8.5 x 21 mm, 23 faces (baked)
FEATURE [Part::Feature] ISO4762_M5x16_002  label="ISO4762_M5x16_018"
  Placement = pos=(877.219,144.849,105.117) rot=(0,0,1;0rad)
  shape: bbox 8.5 x 8.5 x 21 mm, 23 faces (baked)
FEATURE [Part::Feature] ISO4762_M5x16_003  label="ISO4762_M5x16_019"
  Placement = pos=(842.302,144.893,105.299) rot=(0,0,1;0rad)
  shape: bbox 8.5 x 8.5 x 21 mm, 23 faces (baked)
FEATURE [Part::Feature] ISO4762_M5x16_004  label="ISO4762_M5x16_020"
  Placement = pos=(1065.98,109.659,105.239) rot=(0,0,1;0rad)
  shape: bbox 8.5 x 8.5 x 21 mm, 23 faces (baked)
FEATURE [Part::Feature] ISO4762_M5x16_005  label="ISO4762_M5x16_021"
  Placement = pos=(1100.95,144.239,105.117) rot=(0,0,1;0rad)
  shape: bbox 8.5 x 8.5 x 21 mm, 23 faces (baked)
FEATURE [Part::Feature] ISO4762_M5x16_006  label="ISO4762_M5x16_005"
  Placement = pos=(1100.96,109.918,105.186) rot=(0,0,1;0rad)
  shape: bbox 8.5 x 8.5 x 21 mm, 23 faces (baked)
FEATURE [Part::Feature] ISO4762_M5x16_007  label="ISO4762_M5x16_022"
  Placement = pos=(1066.03,144.283,105.299) rot=(0,0,1;0rad)
  shape: bbox 8.5 x 8.5 x 21 mm, 23 faces (baked)
FEATURE [Part::Feature] ISO4762_M5x16_008  label="ISO4762_M5x16_023"
  Placement = pos=(841.521,357.035,105.239) rot=(0,0,1;0rad)
  shape: bbox 8.5 x 8.5 x 21 mm, 23 faces (baked)
FEATURE [Part::Feature] ISO4762_M5x16_009  label="ISO4762_M5x16_024"
  Placement = pos=(876.492,391.615,105.117) rot=(0,0,1;0rad)
  shape: bbox 8.5 x 8.5 x 21 mm, 23 faces (baked)
FEATURE [Part::Feature] ISO4762_M5x16_010  label="ISO4762_M5x16_025"
  Placement = pos=(876.5,357.293,105.186) rot=(0,0,1;0rad)
  shape: bbox 8.5 x 8.5 x 21 mm, 23 faces (baked)
FEATURE [Part::Feature] ISO4762_M5x16_011  label="ISO4762_M5x16_026"
  Placement = pos=(841.575,391.659,105.299) rot=(0,0,1;0rad)
  shape: bbox 8.5 x 8.5 x 21 mm, 23 faces (baked)
FEATURE [Part::Feature] ISO4762_M5x16_012  label="ISO4762_M5x16_027"
  Placement = pos=(1065.93,357.035,105.239) rot=(0,0,1;0rad)
  shape: bbox 8.5 x 8.5 x 21 mm, 23 faces (baked)
FEATURE [Part::Feature] ISO4762_M5x16_013  label="ISO4762_M5x16_028"
  Placement = pos=(1100.9,391.615,105.117) rot=(0,0,1;0rad)
  shape: bbox 8.5 x 8.5 x 21 mm, 23 faces (baked)
FEATURE [Part::Feature] ISO4762_M5x16_014  label="ISO4762_M5x16_013"
  Placement = pos=(1100.91,357.293,105.186) rot=(0,0,1;0rad)
  shape: bbox 8.5 x 8.5 x 21 mm, 23 faces (baked)
FEATURE [Part::Feature] ISO4762_M5x16_015  label="ISO4762_M5x16_029"
  Placement = pos=(1065.98,391.659,105.299) rot=(0,0,1;0rad)
  shape: bbox 8.5 x 8.5 x 21 mm, 23 faces (baked)
FEATURE [App::DocumentObjectGroup] Group002  label="Bed_Base"
  Group = -> [Cut011005,Pocket015,ISO4762_M5x16_,ISO4762_M5x16_006,ISO4762_M5x16_004,ISO4762_M5x16_007,ISO4762_M5x16_002,ISO4762_M5x16_011,ISO4762_M5x16_001,ISO4762_M5x16_005,ISO4762_M5x16_003,ISO4762_M5x16_010,ISO4762_M5x16_009,ISO4762_M5x16_015,ISO4762_M5x16_013,ISO4762_M5x16_008,ISO4762_M5x16_012,ISO4762_M5x16_014]
FEATURE [Part::Feature] Pocket031  label="SBR20UU"
  Placement = pos=(840.2,398.517,60.2) rot=(1,0,0;1.5708rad)
  shape: bbox 48 x 50 x 39 mm, 22 faces (baked)
FEATURE [Part::Feature] Pocket032  label="SBR20UU001"
  Placement = pos=(1058.48,152.4,60.2) rot=(1,0,0;1.5708rad)
  shape: bbox 48 x 50 x 39 mm, 22 faces (baked)
FEATURE [Part::Feature] Pocket033  label="SBR20UU002"
  Placement = pos=(1058.48,399.7,60.2) rot=(1,0,0;1.5708rad)
  shape: bbox 48 x 50 x 39 mm, 22 faces (baked)
FEATURE [Part::Feature] Pocket034  label="SBR20UU003"
  Placement = pos=(840.2,152.4,60.2) rot=(1,0,0;1.5708rad)
  shape: bbox 48 x 50 x 39 mm, 22 faces (baked)
FEATURE [App::DocumentObjectGroup] Group008  label="GuideX"
  Group = -> [Cylinder004,Cylinder005,Pocket031,Pocket032,Pocket033,Pocket034]
